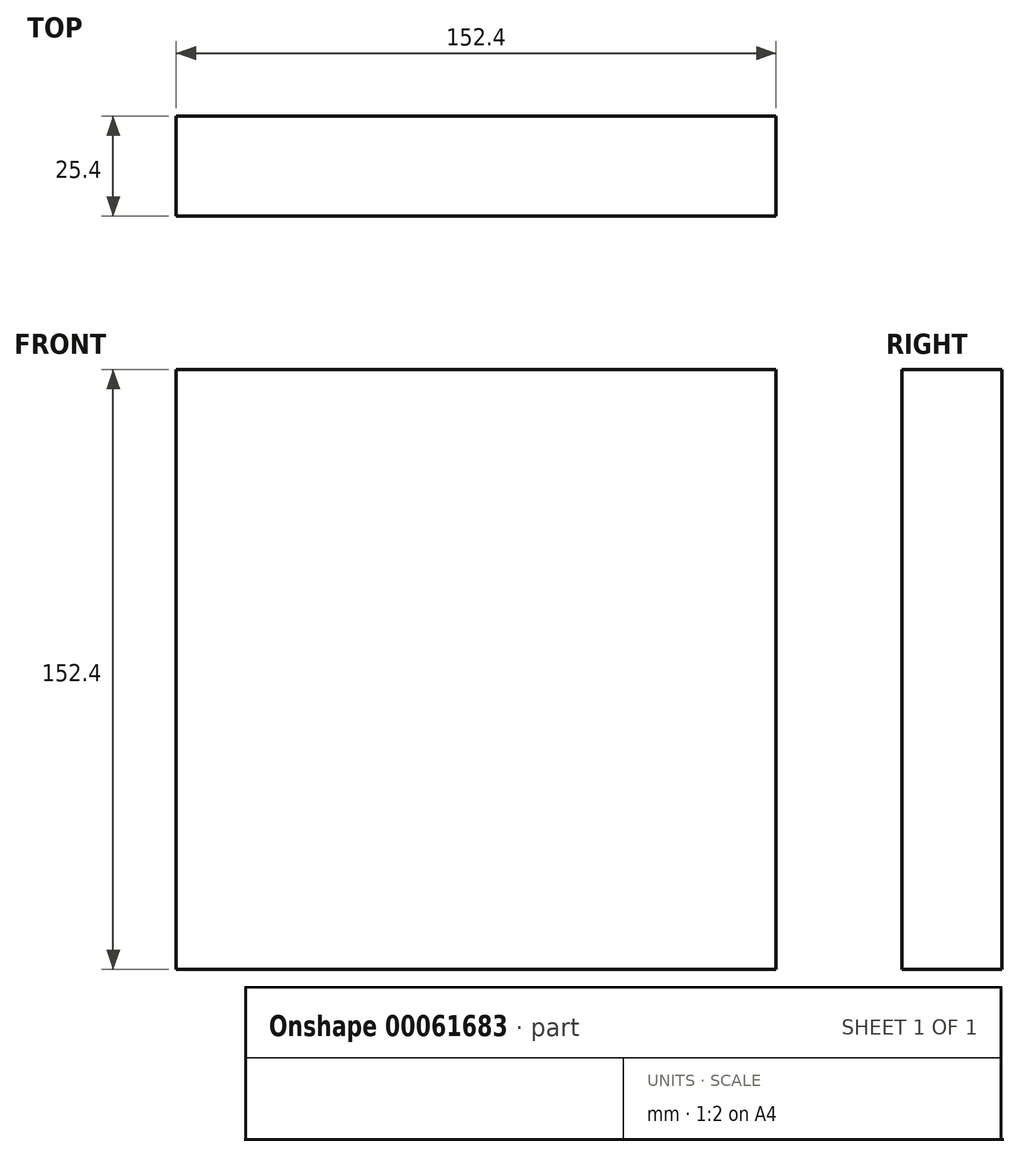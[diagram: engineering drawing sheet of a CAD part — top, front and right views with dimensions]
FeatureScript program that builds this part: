
annotation { "Feature Type Name" : "Feature", "Feature Type Description" : "" }
export const myFeature = defineFeature(function(context is Context, id is Id, definition is map)
    precondition{}
    {
        {
            var Q0;
            Q0=qCreatedBy(makeId("Front.planeOp"),FACE);
            var sketch = newSketch(context, id + "F0", { "sketchPlane" : qUnion([Q0])});
            skLineSegment(sketch, "E0.bottom", {"start": v(-77.22, 84.33) * mm, "end": v(75.18, 84.33) * mm});
            skLineSegment(sketch, "E0.top", {"start": v(-77.22, -68.07) * mm, "end": v(75.18, -68.07) * mm});
            skLineSegment(sketch, "E0.left", {"start": v(-77.22, 84.33) * mm, "end": v(-77.22, -68.07) * mm});
            skLineSegment(sketch, "E0.right", {"start": v(75.18, 84.33) * mm, "end": v(75.18, -68.07) * mm});
            skSolve(sketch);
        }
        {
            var Q0;
            Q0=makeQuery(id+"F0.imprint","IMPRINT",FACE,{"disambiguationData":[TD([[makeQuery(id+"F0.imprint","IMPRINT",EDGE,{"derivedFrom":sQuery(id+"F0.wireOp",EDGE,"E0.bottom")}),-1.0]])]});
            extrude(context, id + "F1", {"entities" : qUnion([Q0]), "depth" : 25.4 * mm});
        }
    });
